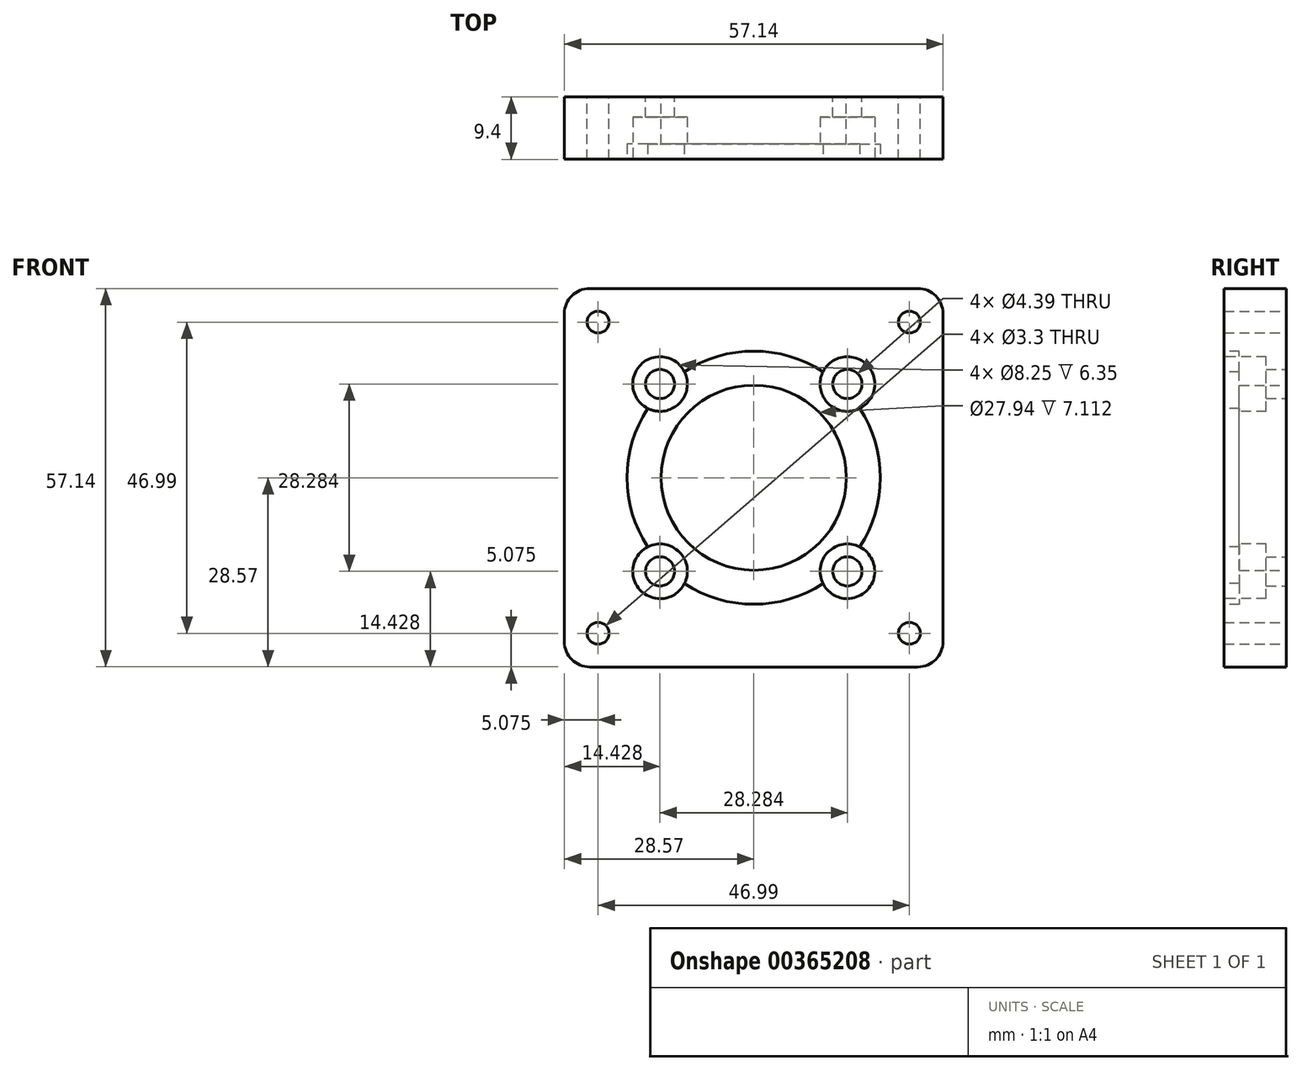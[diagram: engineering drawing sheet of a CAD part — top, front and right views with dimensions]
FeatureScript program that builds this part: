
annotation { "Feature Type Name" : "Feature", "Feature Type Description" : "" }
export const myFeature = defineFeature(function(context is Context, id is Id, definition is map)
    precondition{}
    {
        {
            var Q0;
            Q0=qCreatedBy(makeId("Front.planeOp"),FACE);
            var sketch = newSketch(context, id + "F0", { "sketchPlane" : qUnion([Q0])});
            skLineSegment(sketch, "E0.bottom", {"start": v(28.58, -28.57) * mm, "end": v(-28.57, -28.58) * mm});
            skLineSegment(sketch, "E0.top", {"start": v(28.57, 28.58) * mm, "end": v(-28.58, 28.58) * mm});
            skLineSegment(sketch, "E0.left", {"start": v(28.58, -28.57) * mm, "end": v(28.57, 28.58) * mm});
            skLineSegment(sketch, "E0.right", {"start": v(-28.57, -28.58) * mm, "end": v(-28.58, 28.58) * mm});
            skPoint(sketch, "E0.middle", {"position": v(0, 0) * mm});
            skCircle(sketch, "E1", {"center": v(0, 0) * mm, "radius": 13.97 * mm});
            skCircle(sketch, "E2", {"center": v(0, 0) * mm, "radius": 20 * mm, "construction": true});
            skLineSegment(sketch, "E3", {"start": v(0, 0) * mm, "end": v(-28.57, -28.57) * mm, "construction": true});
            skCircle(sketch, "E4", {"center": v(-23.5, -23.5) * mm, "radius": 1.65 * mm});
            skCircle(sketch, "E5", {"center": v(-14.14, -14.14) * mm, "radius": 2.2 * mm});
            skCircle(sketch, "E6.MirrorC", {"center": v(-14.14, 14.14) * mm, "radius": 2.2 * mm});
            skCircle(sketch, "E7.MirrorC", {"center": v(-23.5, 23.5) * mm, "radius": 1.65 * mm});
            skCircle(sketch, "E8.MirrorC", {"center": v(23.5, 23.5) * mm, "radius": 1.65 * mm});
            skCircle(sketch, "E9.MirrorC", {"center": v(23.5, -23.5) * mm, "radius": 1.65 * mm});
            skCircle(sketch, "E10.MirrorC", {"center": v(14.14, -14.14) * mm, "radius": 2.2 * mm});
            skCircle(sketch, "E11.MirrorC", {"center": v(14.14, 14.14) * mm, "radius": 2.2 * mm});
            skSolve(sketch);
        }
        {
            var Q0;
            Q0=makeQuery(id+"F0.imprint","IMPRINT",FACE,{"disambiguationData":[TD([[makeQuery(id+"F0.imprint","IMPRINT",EDGE,{"derivedFrom":sQuery(id+"F0.wireOp",EDGE,"E0.bottom")}),-1.0]])]});
            extrude(context, id + "F1", {"entities" : qUnion([Q0]), "depth" : 9.4 * mm});
        }
        {
            var Q0;
            Q0=makeQuery(id+"F1.opExtrude","CAP_FACE",FACE,{"disambiguationData":[OSD([sQuery(id+"F0.wireOp",EDGE,"E0.bottom"),sQuery(id+"F0.wireOp",EDGE,"E0.top"),sQuery(id+"F0.wireOp",EDGE,"E0.left"),sQuery(id+"F0.wireOp",EDGE,"E0.right"),sQuery(id+"F0.wireOp",EDGE,"E1"),sQuery(id+"F0.wireOp",EDGE,"E6.MirrorC"),sQuery(id+"F0.wireOp",EDGE,"E4"),sQuery(id+"F0.wireOp",EDGE,"E7.MirrorC"),sQuery(id+"F0.wireOp",EDGE,"E5"),sQuery(id+"F0.wireOp",EDGE,"E10.MirrorC"),sQuery(id+"F0.wireOp",EDGE,"E11.MirrorC"),sQuery(id+"F0.wireOp",EDGE,"E9.MirrorC"),sQuery(id+"F0.wireOp",EDGE,"E8.MirrorC")])],"isStart":false});
            var sketch = newSketch(context, id + "F2", { "sketchPlane" : qUnion([Q0])});
            skCircle(sketch, "E12", {"center": v(-14.14, 14.14) * mm, "radius": 4.12 * mm});
            skCircle(sketch, "E13", {"center": v(-14.14, -14.14) * mm, "radius": 4.12 * mm});
            skCircle(sketch, "E14", {"center": v(14.14, 14.14) * mm, "radius": 4.12 * mm});
            skCircle(sketch, "E15", {"center": v(14.14, -14.14) * mm, "radius": 4.12 * mm});
            skSolve(sketch);
        }
        {
            var Q0;
            Q0=makeQuery(id+"F2.imprint","IMPRINT",FACE,{"disambiguationData":[TD([[makeQuery(id+"F2.imprint","IMPRINT",EDGE,{"derivedFrom":sQuery(id+"F2.wireOp",EDGE,"E12")}),1.0]])]});
            var Q1;
            Q1=makeQuery(id+"F2.imprint","IMPRINT",FACE,{"disambiguationData":[TD([[makeQuery(id+"F2.imprint","IMPRINT",EDGE,{"derivedFrom":sQuery(id+"F2.wireOp",EDGE,"E14")}),1.0]])]});
            var Q2;
            Q2=makeQuery(id+"F2.imprint","IMPRINT",FACE,{"disambiguationData":[TD([[makeQuery(id+"F2.imprint","IMPRINT",EDGE,{"derivedFrom":sQuery(id+"F2.wireOp",EDGE,"E15")}),1.0]])]});
            var Q3;
            Q3=makeQuery(id+"F2.imprint","IMPRINT",FACE,{"disambiguationData":[TD([[makeQuery(id+"F2.imprint","IMPRINT",EDGE,{"derivedFrom":sQuery(id+"F2.wireOp",EDGE,"E13")}),1.0]])]});
            var Q4;
            Q4=sQuery(id+"F2.wireOp",EDGE,"E12");
            var Q5;
            Q5=sQuery(id+"F2.wireOp",EDGE,"E14");
            var Q6;
            Q6=sQuery(id+"F2.wireOp",EDGE,"E13");
            var Q7;
            Q7=sQuery(id+"F2.wireOp",EDGE,"E15");
            extrude(context, id + "F3", {"entities" : qUnion([Q0, Q1, Q2, Q3]), "operationType" : NewBodyOperationType.REMOVE, "surfaceEntities" : qUnion([Q4, Q5, Q6, Q7]), "oppositeDirection" : true, "depth" : 6.35 * mm, "offsetDistance" : 25.4 * mm});
        }
        {
            var Q0;
            Q0=makeQuery(id+"F1.opExtrude","CAP_FACE",FACE,{"disambiguationData":[OSD([sQuery(id+"F0.wireOp",EDGE,"E0.bottom"),sQuery(id+"F0.wireOp",EDGE,"E0.top"),sQuery(id+"F0.wireOp",EDGE,"E0.left"),sQuery(id+"F0.wireOp",EDGE,"E0.right"),sQuery(id+"F0.wireOp",EDGE,"E1"),sQuery(id+"F0.wireOp",EDGE,"E6.MirrorC"),sQuery(id+"F0.wireOp",EDGE,"E4"),sQuery(id+"F0.wireOp",EDGE,"E7.MirrorC"),sQuery(id+"F0.wireOp",EDGE,"E5"),sQuery(id+"F0.wireOp",EDGE,"E10.MirrorC"),sQuery(id+"F0.wireOp",EDGE,"E11.MirrorC"),sQuery(id+"F0.wireOp",EDGE,"E9.MirrorC"),sQuery(id+"F0.wireOp",EDGE,"E8.MirrorC")])],"isStart":false});
            var sketch = newSketch(context, id + "F4", { "sketchPlane" : qUnion([Q0])});
            skCircle(sketch, "E16", {"center": v(0, 0) * mm, "radius": 19.11 * mm});
            skSolve(sketch);
        }
        {
            var Q0;
            Q0=makeQuery(id+"F4.imprint","IMPRINT",FACE,{"disambiguationData":[TD([[makeQuery(id+"F4.imprint","IMPRINT",EDGE,{"derivedFrom":makeQuery(id+"F1.opExtrude","CAP_EDGE",EDGE,{"disambiguationData":[OSD([sQuery(id+"F0.wireOp",EDGE,"E1")])],"isStart":false})}),-1.0]])]});
            extrude(context, id + "F5", {"entities" : qUnion([Q0]), "operationType" : NewBodyOperationType.REMOVE, "oppositeDirection" : true, "depth" : 2.3 * mm, "offsetDistance" : 25.4 * mm});
        }
        {
            var Q0;
            Q0=makeQuery(id+"F1.opExtrude","SWEPT_EDGE",EDGE,{"disambiguationData":[OSD([sQuery(id+"F0.wireOp",EDGE,"E0.top"),sQuery(id+"F0.wireOp",EDGE,"E0.right")])]});
            var Q1;
            Q1=makeQuery(id+"F1.opExtrude","SWEPT_EDGE",EDGE,{"disambiguationData":[OSD([sQuery(id+"F0.wireOp",EDGE,"E0.top"),sQuery(id+"F0.wireOp",EDGE,"E0.left")])]});
            var Q2;
            Q2=makeQuery(id+"F1.opExtrude","SWEPT_EDGE",EDGE,{"disambiguationData":[OSD([sQuery(id+"F0.wireOp",EDGE,"E0.bottom"),sQuery(id+"F0.wireOp",EDGE,"E0.left")])]});
            var Q3;
            Q3=makeQuery(id+"F1.opExtrude","SWEPT_EDGE",EDGE,{"disambiguationData":[OSD([sQuery(id+"F0.wireOp",EDGE,"E0.bottom"),sQuery(id+"F0.wireOp",EDGE,"E0.right")])]});
            fillet(context, id + "F6", {"entities" : qUnion([Q0, Q1, Q2, Q3]), "radius" : 3.8 * mm, "allowEdgeOverflow" : false});
        }
    });
